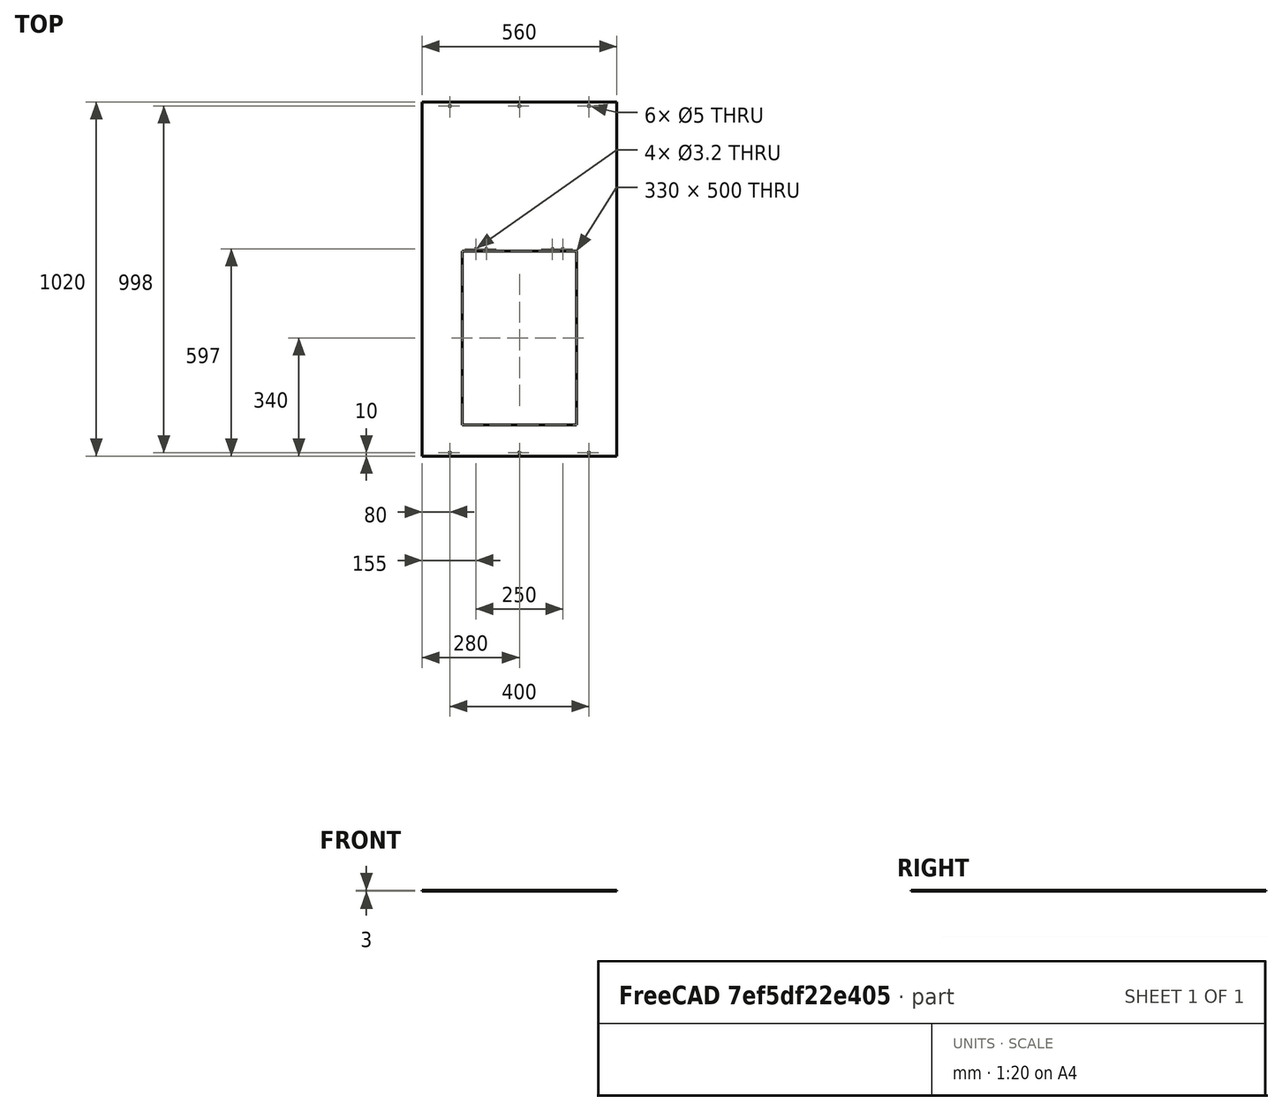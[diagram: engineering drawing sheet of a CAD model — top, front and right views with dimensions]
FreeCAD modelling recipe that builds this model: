
FCSTD DOCUMENT  (FreeCAD 0.16R6706 (Git))
Label: frame_cover_door
License: CreativeCommons Attribution-ShareAlike
LicenseURL: http://creativecommons.org/licenses/by-sa/4.0/
objects: Sketcher::SketchObject×1, PartDesign::Pad×1
note: 3 computed .brp shape members not serialized (recipe doc carries the construction recipe); baked Part::Feature solids carry a one-line shape summary decoded from their .brp

FEATURE [Sketcher::SketchObject] Sketch
  sketch-geometry (21):
    g0: LineSegment StartX=0 StartY=0 StartZ=0 EndX=560 EndY=0 EndZ=0
    g1: LineSegment StartX=560 StartY=0 StartZ=0 EndX=560 EndY=1020 EndZ=0
    g2: LineSegment StartX=560 StartY=1020 StartZ=0 EndX=0 EndY=1020 EndZ=0
    g3: LineSegment StartX=0 StartY=1020 StartZ=0 EndX=0 EndY=0 EndZ=0
    g4: Circle CenterX=80 CenterY=1008 CenterZ=0 NormalX=0 NormalY=0 NormalZ=1 Radius=2.5
    g5: Circle CenterX=280 CenterY=1008 CenterZ=0 NormalX=0 NormalY=0 NormalZ=1 Radius=2.5
    g6: Circle CenterX=480 CenterY=1008 CenterZ=0 NormalX=0 NormalY=0 NormalZ=1 Radius=2.5
    g7: LineSegment [constr] StartX=0 StartY=1008 StartZ=0 EndX=560 EndY=1008 EndZ=0
    g8: LineSegment [constr] StartX=0 StartY=10 StartZ=0 EndX=560 EndY=10 EndZ=0
    g9: Circle CenterX=80 CenterY=10 CenterZ=0 NormalX=0 NormalY=0 NormalZ=1 Radius=2.5
    g10: Circle CenterX=280 CenterY=10 CenterZ=0 NormalX=0 NormalY=0 NormalZ=1 Radius=2.5
    g11: Circle CenterX=480 CenterY=10 CenterZ=0 NormalX=0 NormalY=0 NormalZ=1 Radius=2.5
    g12: LineSegment StartX=115 StartY=590 StartZ=0 EndX=445 EndY=590 EndZ=0
    g13: LineSegment StartX=445 StartY=590 StartZ=0 EndX=445 EndY=90 EndZ=0
    g14: LineSegment StartX=445 StartY=90 StartZ=0 EndX=115 EndY=90 EndZ=0
    g15: LineSegment StartX=115 StartY=90 StartZ=0 EndX=115 EndY=590 EndZ=0
    g16: Circle CenterX=405 CenterY=597 CenterZ=0 NormalX=0 NormalY=0 NormalZ=1 Radius=1.6
    g17: Circle CenterX=155 CenterY=597 CenterZ=0 NormalX=0 NormalY=0 NormalZ=1 Radius=1.6
    g18: Circle CenterX=185 CenterY=597 CenterZ=0 NormalX=0 NormalY=0 NormalZ=1 Radius=1.6
    g19: Circle CenterX=375 CenterY=597 CenterZ=0 NormalX=0 NormalY=0 NormalZ=1 Radius=1.6
    g20: LineSegment [constr] StartX=405 StartY=597 StartZ=0 EndX=155 EndY=597 EndZ=0
  constraints (63):
    c: Coincident(g0,g1)
    c: Coincident(g1,g2)
    c: Coincident(g2,g3)
    c: Coincident(g3,g0)
    c: Horizontal(g0)
    c: Horizontal(g2)
    c: Vertical(g1)
    c: Vertical(g3)
    c: Coincident(g0,g-1)
    c: DistanceY(g1,g1) = 1020
    c: DistanceX(g2,g2) = 560
    c: PointOnObject(g7,g3)
    c: Horizontal(g7)
    c: PointOnObject(g6,g7)
    c: PointOnObject(g5,g7)
    c: PointOnObject(g4,g7)
    c: DistanceY(g7,g1) = 12
    c: PointOnObject(g7,g1)
    c: DistanceX(g2,g4) = 80
    c: DistanceX(g6,g1) = 80
    c: DistanceX(g4,g5) = 200
    c: Equal(g4,g5)
    c: Equal(g5,g6)
    c: Radius(g6) = 2.5
    c: PointOnObject(g8,g3)
    c: PointOnObject(g8,g1)
    c: Horizontal(g8)
    c: DistanceY(g0,g8) = 10
    c: PointOnObject(g9,g8)
    c: PointOnObject(g10,g8)
    c: PointOnObject(g11,g8)
    c: DistanceX(g11,g0) = 80
    c: DistanceX(g-1,g9) = 80
    c: DistanceX(g9,g10) = 200
    c: Equal(g10,g9)
    c: Equal(g9,g11)
    c: Radius(g10) = 2.5
    c: Coincident(g12,g13)
    c: Coincident(g13,g14)
    c: Coincident(g14,g15)
    c: Coincident(g15,g12)
    c: Horizontal(g12)
    c: Horizontal(g14)
    c: Vertical(g13)
    c: Vertical(g15)
    c: DistanceY(g13,g13) = 500
    c: DistanceX(g12,g12) = 330
    c: DistanceY(g-1,g14) = 90
    c: DistanceX(g-1,g14) = 115
    c: Coincident(g20,g16)
    c: Coincident(g20,g17)
    c: Horizontal(g20)
    c: PointOnObject(g18,g20)
    c: PointOnObject(g19,g20)
    c: Equal(g19,g16)
    c: Equal(g16,g18)
    c: Equal(g18,g17)
    c: Radius(g19) = 1.6
    c: DistanceX(g16,g12) = 40
    c: DistanceX(g12,g17) = 40
    c: DistanceX(g17,g18) = 30
    c: DistanceX(g19,g16) = 30
    c: DistanceY(g12,g17) = 7
FEATURE [PartDesign::Pad] Pad
  Length = 3
  Length2 = 100
  Sketch = -> Sketch
  Type = 0
